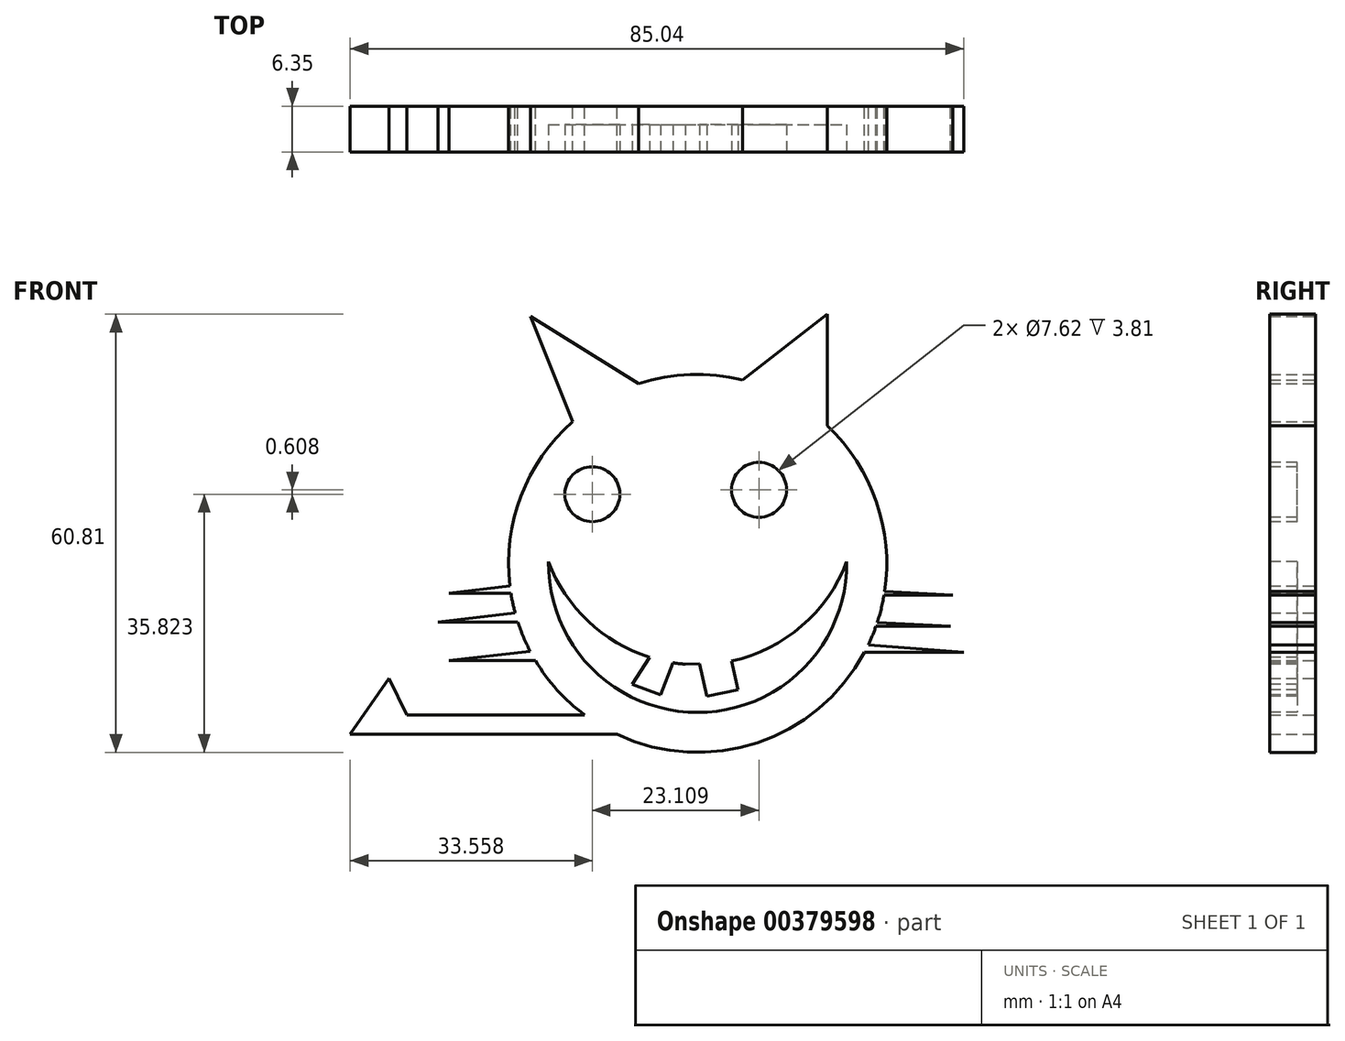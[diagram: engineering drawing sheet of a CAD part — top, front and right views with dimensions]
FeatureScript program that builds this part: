
annotation { "Feature Type Name" : "Feature", "Feature Type Description" : "" }
export const myFeature = defineFeature(function(context is Context, id is Id, definition is map)
    precondition{}
    {
        {
            var Q0;
            Q0=qCreatedBy(makeId("Front.planeOp"),FACE);
            var sketch = newSketch(context, id + "F0", { "sketchPlane" : qUnion([Q0])});
            skArc(sketch, "E0", {"start": v(-17.35, 19.66) * mm, "mid": v(-24.5, 9.36) * mm, "end": v(-26.04, -3.09) * mm});
            skLineSegment(sketch, "E1", {"start": v(-17.35, 19.66) * mm, "end": v(-23.16, 34.3) * mm});
            skLineSegment(sketch, "E2", {"start": v(-23.16, 34.3) * mm, "end": v(-8.16, 24.92) * mm});
            skLineSegment(sketch, "E3", {"start": v(6.21, 25.47) * mm, "end": v(17.98, 34.6) * mm});
            skLineSegment(sketch, "E4", {"start": v(17.98, 34.6) * mm, "end": v(17.98, 19.08) * mm});
            skLineSegment(sketch, "E5", {"start": v(25.84, -4.41) * mm, "end": v(35.36, -4.41) * mm});
            skLineSegment(sketch, "E6", {"start": v(24.73, -8.7) * mm, "end": v(35.05, -8.7) * mm});
            skLineSegment(sketch, "E7", {"start": v(23.14, -12.33) * mm, "end": v(36.88, -12.33) * mm});
            skLineSegment(sketch, "E8", {"start": v(-25.9, -4.11) * mm, "end": v(-34.44, -4.11) * mm});
            skLineSegment(sketch, "E9", {"start": v(-24.92, -8.14) * mm, "end": v(-35.97, -8.14) * mm});
            skLineSegment(sketch, "E10", {"start": v(-22.48, -13.49) * mm, "end": v(-34.44, -13.49) * mm});
            skLineSegment(sketch, "E11", {"start": v(-11.19, -23.71) * mm, "end": v(-48.16, -23.71) * mm});
            skLineSegment(sketch, "E12", {"start": v(-48.16, -23.71) * mm, "end": v(-42.8, -15.92) * mm});
            skArc(sketch, "E13.trimOffspring", {"start": v(6.21, 25.47) * mm, "mid": v(-1.01, 26.2) * mm, "end": v(-8.16, 24.92) * mm});
            skLineSegment(sketch, "E14", {"start": v(35.36, -4.41) * mm, "end": v(25.93, -3.9) * mm});
            skArc(sketch, "E15.trimOffspring", {"start": v(25.93, -3.9) * mm, "mid": v(24.78, 8.56) * mm, "end": v(17.98, 19.08) * mm});
            skLineSegment(sketch, "E16", {"start": v(35.05, -8.7) * mm, "end": v(24.9, -8.22) * mm});
            skArc(sketch, "E17.trimOffspring", {"start": v(24.9, -8.22) * mm, "mid": v(25.44, -6.33) * mm, "end": v(25.84, -4.41) * mm});
            skLineSegment(sketch, "E18", {"start": v(36.88, -12.33) * mm, "end": v(23.66, -11.3) * mm});
            skArc(sketch, "E19.trimOffspring", {"start": v(23.66, -11.3) * mm, "mid": v(24.23, -10.01) * mm, "end": v(24.73, -8.7) * mm});
            skLineSegment(sketch, "E20", {"start": v(-34.44, -13.49) * mm, "end": v(-23.2, -12.2) * mm});
            skArc(sketch, "E21.trimOffspring", {"start": v(-22.48, -13.49) * mm, "mid": v(-19.46, -17.58) * mm, "end": v(-15.7, -21) * mm});
            skLineSegment(sketch, "E22", {"start": v(-35.97, -8.14) * mm, "end": v(-25.31, -6.84) * mm});
            skArc(sketch, "E23.trimOffspring", {"start": v(-24.92, -8.14) * mm, "mid": v(-24.15, -10.2) * mm, "end": v(-23.2, -12.2) * mm});
            skLineSegment(sketch, "E24", {"start": v(-34.44, -4.11) * mm, "end": v(-26.04, -3.09) * mm});
            skArc(sketch, "E25.trimOffspring", {"start": v(-25.9, -4.11) * mm, "mid": v(-25.64, -5.48) * mm, "end": v(-25.31, -6.84) * mm});
            skLineSegment(sketch, "E26", {"start": v(-42.8, -15.92) * mm, "end": v(-40.34, -21) * mm});
            skLineSegment(sketch, "E27", {"start": v(-40.34, -21) * mm, "end": v(-15.7, -21) * mm});
            skArc(sketch, "E28.trimOffspring", {"start": v(-11.19, -23.71) * mm, "mid": v(8.25, -24.89) * mm, "end": v(23.14, -12.33) * mm});
            skSolve(sketch);
        }
        {
            var Q0;
            Q0=makeQuery(id+"F0.imprint","IMPRINT",FACE,{"disambiguationData":[TD([[makeQuery(id+"F0.imprint","IMPRINT",EDGE,{"derivedFrom":sQuery(id+"F0.wireOp",EDGE,"E0")}),1.0]])]});
            extrude(context, id + "F1", {"entities" : qUnion([Q0]), "depth" : 6.35 * mm});
        }
        {
            var Q0;
            Q0=makeQuery(id+"F1.opExtrude","CAP_FACE",FACE,{"disambiguationData":[OSD([sQuery(id+"F0.wireOp",EDGE,"E0")])],"isStart":false});
            var sketch = newSketch(context, id + "F2", { "sketchPlane" : qUnion([Q0])});
            skCircle(sketch, "E29", {"center": v(-14.6, 9.6) * mm, "radius": 3.81 * mm});
            skCircle(sketch, "E30", {"center": v(8.5, 10.21) * mm, "radius": 3.81 * mm});
            skArc(sketch, "E31", {"start": v(-20.67, 0.22) * mm, "mid": v(-15.2, -8) * mm, "end": v(-6.68, -13.02) * mm});
            skArc(sketch, "E32.trimOffspring", {"start": v(-20.67, 0.22) * mm, "mid": v(0, -20.67) * mm, "end": v(20.67, 0.22) * mm});
            skLineSegment(sketch, "E33", {"start": v(-1.72, -13.98) * mm, "end": v(0.28, -13.9) * mm});
            skArc(sketch, "E34.trimOffspring", {"start": v(3.7, -13.74) * mm, "mid": v(14.05, -9.01) * mm, "end": v(20.67, 0.22) * mm});
            skLineSegment(sketch, "E35", {"start": v(4.74, -13.54) * mm, "end": v(5.6, -17.51) * mm});
            skLineSegment(sketch, "E36", {"start": v(5.6, -17.51) * mm, "end": v(1.26, -18.45) * mm});
            skLineSegment(sketch, "E37", {"start": v(1.26, -18.45) * mm, "end": v(0.25, -13.74) * mm});
            skLineSegment(sketch, "E38", {"start": v(-6.68, -13.02) * mm, "end": v(-9.04, -16.77) * mm});
            skLineSegment(sketch, "E39", {"start": v(-9.04, -16.77) * mm, "end": v(-5.15, -18.25) * mm});
            skLineSegment(sketch, "E40", {"start": v(-5.15, -18.25) * mm, "end": v(-3.45, -13.78) * mm});
            skArc(sketch, "E41.trimOffspring", {"start": v(-3.45, -13.78) * mm, "mid": v(-2.59, -13.9) * mm, "end": v(-1.72, -13.98) * mm});
            skSolve(sketch);
        }
        {
            var Q0;
            Q0=makeQuery(id+"F2.imprint","IMPRINT",FACE,{"disambiguationData":[TD([[makeQuery(id+"F2.imprint","IMPRINT",EDGE,{"derivedFrom":sQuery(id+"F2.wireOp",EDGE,"E30")}),1.0]])]});
            var Q1;
            Q1=makeQuery(id+"F2.imprint","IMPRINT",FACE,{"disambiguationData":[TD([[makeQuery(id+"F2.imprint","IMPRINT",EDGE,{"derivedFrom":sQuery(id+"F2.wireOp",EDGE,"E29")}),1.0]])]});
            var Q2;
            Q2=makeQuery(id+"F2.imprint","IMPRINT",FACE,{"disambiguationData":[TD([[makeQuery(id+"F2.imprint","IMPRINT",EDGE,{"derivedFrom":sQuery(id+"F2.wireOp",EDGE,"E31")}),-1.0]])]});
            extrude(context, id + "F3", {"entities" : qUnion([Q0, Q1, Q2]), "operationType" : NewBodyOperationType.REMOVE, "oppositeDirection" : true, "depth" : 3.8 * mm});
        }
    });
